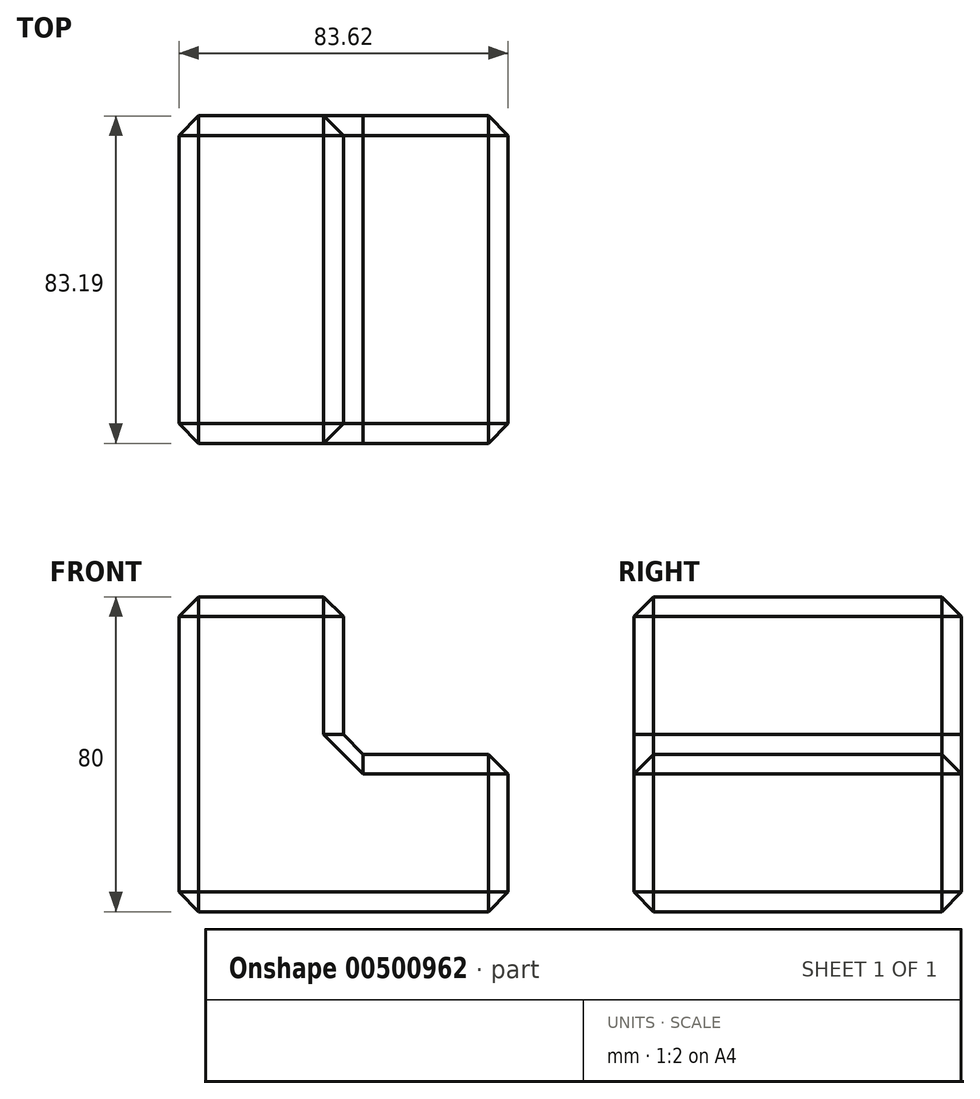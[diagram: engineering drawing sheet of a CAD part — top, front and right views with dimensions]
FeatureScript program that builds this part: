
annotation { "Feature Type Name" : "Feature", "Feature Type Description" : "" }
export const myFeature = defineFeature(function(context is Context, id is Id, definition is map)
    precondition{}
    {
        {
            var Q0;
            Q0=qCreatedBy(makeId("Top.planeOp"),FACE);
            var sketch = newSketch(context, id + "F0", { "sketchPlane" : qUnion([Q0])});
            skLineSegment(sketch, "E0.bottom", {"start": v(-59.13, -45.93) * mm, "end": v(24.5, -45.93) * mm});
            skLineSegment(sketch, "E0.top", {"start": v(-59.13, 37.26) * mm, "end": v(24.5, 37.26) * mm});
            skLineSegment(sketch, "E0.left", {"start": v(-59.13, -45.93) * mm, "end": v(-59.13, 37.26) * mm});
            skLineSegment(sketch, "E0.right", {"start": v(24.5, -45.93) * mm, "end": v(24.5, 37.26) * mm});
            skSolve(sketch);
        }
        {
            var Q0;
            Q0=makeQuery(id+"F0.imprint","IMPRINT",FACE,{"disambiguationData":[TD([[makeQuery(id+"F0.imprint","IMPRINT",EDGE,{"derivedFrom":sQuery(id+"F0.wireOp",EDGE,"E0.bottom")}),1.0]])]});
            extrude(context, id + "F1", {"entities" : qUnion([Q0]), "depth" : 40 * mm});
        }
        {
            var Q0;
            Q0=makeQuery(id+"F1.opExtrude","CAP_FACE",FACE,{"disambiguationData":[OSD([sQuery(id+"F0.wireOp",EDGE,"E0.bottom"),sQuery(id+"F0.wireOp",EDGE,"E0.top"),sQuery(id+"F0.wireOp",EDGE,"E0.left"),sQuery(id+"F0.wireOp",EDGE,"E0.right")])],"isStart":false});
            var sketch = newSketch(context, id + "F2", { "sketchPlane" : qUnion([Q0])});
            skLineSegment(sketch, "E1", {"start": v(-17.32, 37.26) * mm, "end": v(-17.32, -45.93) * mm});
            skSolve(sketch);
        }
        {
            var Q0;
            {var subQ1=sQuery(id+"F2.wireOp",EDGE,"E1");Q0=makeQuery(id+"F2.imprint","IMPRINT",FACE,{"disambiguationData":[TD([[makeQuery(id+"F2.imprint","IMPRINT",EDGE,{"derivedFrom":subQ1}),-1.0]])]});}
            extrude(context, id + "F3", {"entities" : qUnion([Q0]), "operationType" : NewBodyOperationType.ADD, "depth" : 40 * mm});
        }
        {
            var Q0;
            Q0=makeQuery(id+"F3.opExtrude","CAP_FACE",FACE,{"disambiguationData":[OSD([sQuery(id+"F0.wireOp",EDGE,"E0.bottom"),sQuery(id+"F0.wireOp",EDGE,"E0.top"),sQuery(id+"F0.wireOp",EDGE,"E0.left"),sQuery(id+"F2.wireOp",EDGE,"E1")])],"isStart":false});
            var Q1;
            {var subQ0=sQuery(id+"F0.wireOp",EDGE,"E0.bottom");Q1=makeQuery(id+"F3.boolean.opBoolean","MERGE",FACE,{"derivedFrom":[makeQuery(id+"F1.opExtrude","SWEPT_FACE",FACE,{"disambiguationData":[OSD([subQ0])]}),makeQuery(id+"F3.opExtrude","SWEPT_FACE",FACE,{"disambiguationData":[OSD([subQ0])]})]});}
            var Q2;
            Q2=makeQuery(id+"F1.opExtrude","CAP_FACE",FACE,{"disambiguationData":[OSD([sQuery(id+"F0.wireOp",EDGE,"E0.bottom"),sQuery(id+"F0.wireOp",EDGE,"E0.top"),sQuery(id+"F0.wireOp",EDGE,"E0.left"),sQuery(id+"F0.wireOp",EDGE,"E0.right")])],"isStart":false});
            var Q3;
            Q3=makeQuery(id+"F1.opExtrude","SWEPT_FACE",FACE,{"disambiguationData":[OSD([sQuery(id+"F0.wireOp",EDGE,"E0.right")])]});
            var Q4;
            {var subQ0=sQuery(id+"F0.wireOp",EDGE,"E0.top");Q4=makeQuery(id+"F3.boolean.opBoolean","MERGE",FACE,{"derivedFrom":[makeQuery(id+"F1.opExtrude","SWEPT_FACE",FACE,{"disambiguationData":[OSD([subQ0])]}),makeQuery(id+"F3.opExtrude","SWEPT_FACE",FACE,{"disambiguationData":[OSD([subQ0])]})]});}
            var Q5;
            Q5=makeQuery(id+"F1.opExtrude","CAP_FACE",FACE,{"disambiguationData":[OSD([sQuery(id+"F0.wireOp",EDGE,"E0.bottom"),sQuery(id+"F0.wireOp",EDGE,"E0.top"),sQuery(id+"F0.wireOp",EDGE,"E0.left"),sQuery(id+"F0.wireOp",EDGE,"E0.right")])],"isStart":true});
            var Q6;
            {var subQ0=sQuery(id+"F0.wireOp",EDGE,"E0.left");Q6=makeQuery(id+"F3.boolean.opBoolean","MERGE",FACE,{"derivedFrom":[makeQuery(id+"F1.opExtrude","SWEPT_FACE",FACE,{"disambiguationData":[OSD([subQ0])]}),makeQuery(id+"F3.opExtrude","SWEPT_FACE",FACE,{"disambiguationData":[OSD([subQ0])]})]});}
            chamfer(context, id + "F4", {"entities" : qUnion([Q0, Q1, Q2, Q3, Q4, Q5, Q6]), "width" : 5 * mm, "tangentPropagation" : true});
        }
    });
